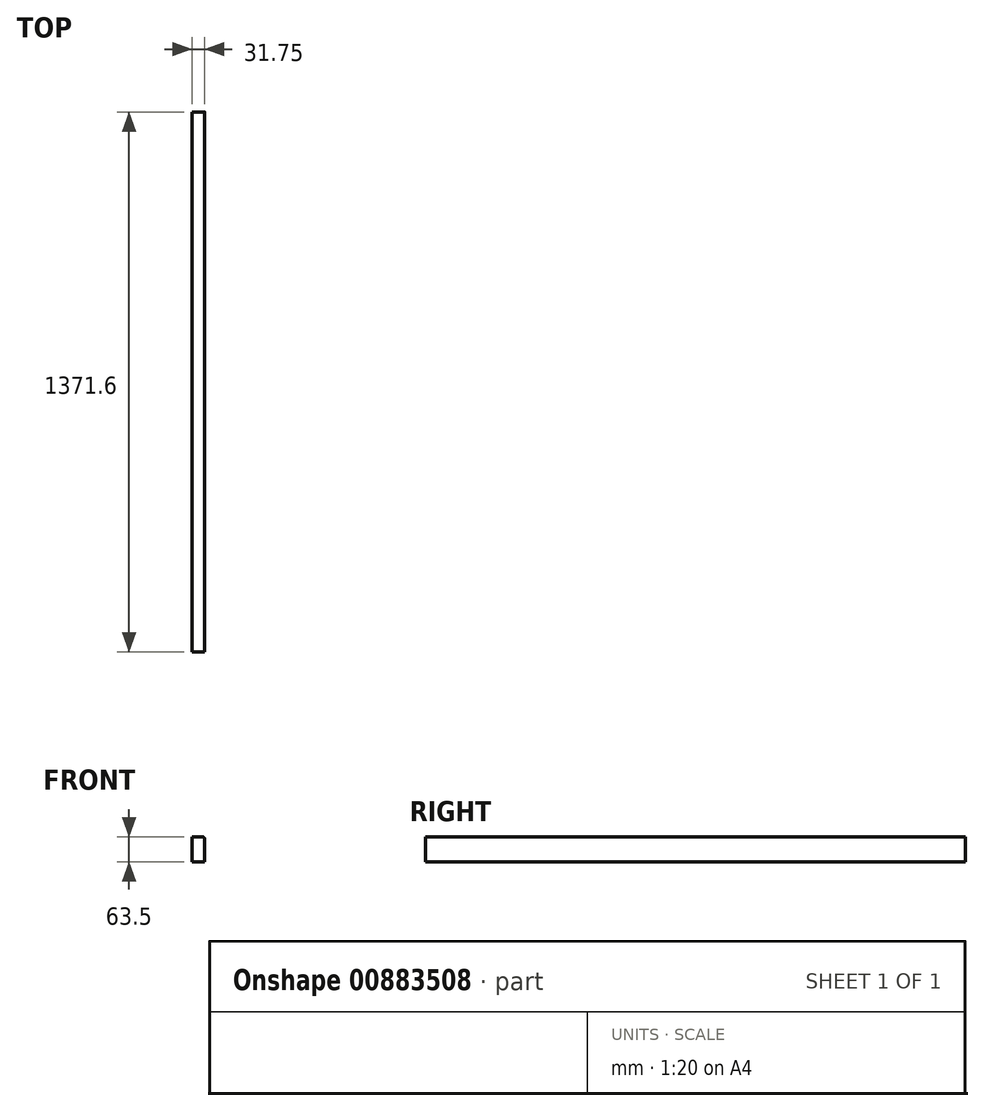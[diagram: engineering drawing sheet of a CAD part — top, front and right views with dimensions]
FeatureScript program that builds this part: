
annotation { "Feature Type Name" : "Feature", "Feature Type Description" : "" }
export const myFeature = defineFeature(function(context is Context, id is Id, definition is map)
    precondition{}
    {
        {
            var Q0;
            Q0=qCreatedBy(makeId("Front.planeOp"),FACE);
            var sketch = newSketch(context, id + "F0", { "sketchPlane" : qUnion([Q0])});
            skLineSegment(sketch, "E0.bottom", {"start": v(0, 0) * mm, "end": v(31.75, 0) * mm});
            skLineSegment(sketch, "E0.top", {"start": v(0, 63.5) * mm, "end": v(31.75, 63.5) * mm});
            skLineSegment(sketch, "E0.left", {"start": v(0, 0) * mm, "end": v(0, 63.5) * mm});
            skLineSegment(sketch, "E0.right", {"start": v(31.75, 0) * mm, "end": v(31.75, 63.5) * mm});
            skSolve(sketch);
        }
        {
            var Q0;
            Q0=qSketchRegion(id+"F0",true);
            extrude(context, id + "F1", {"entities" : qUnion([Q0]), "oppositeDirection" : true, "depth" : 1371.6 * mm, "offsetDistance" : 25.4 * mm});
        }
        {
            var Q0;
            Q0=makeQuery(id+"F1.opExtrude","SWEPT_EDGE",EDGE,{"disambiguationData":[OSD([sQuery(id+"F0.wireOp",EDGE,"E0.top"),sQuery(id+"F0.wireOp",EDGE,"E0.right")])]});
            fillet(context, id + "F2", {"entities" : qUnion([Q0]), "radius" : 5.08 * mm, "tangentPropagation" : true, "allowEdgeOverflow" : false});
        }
    });
